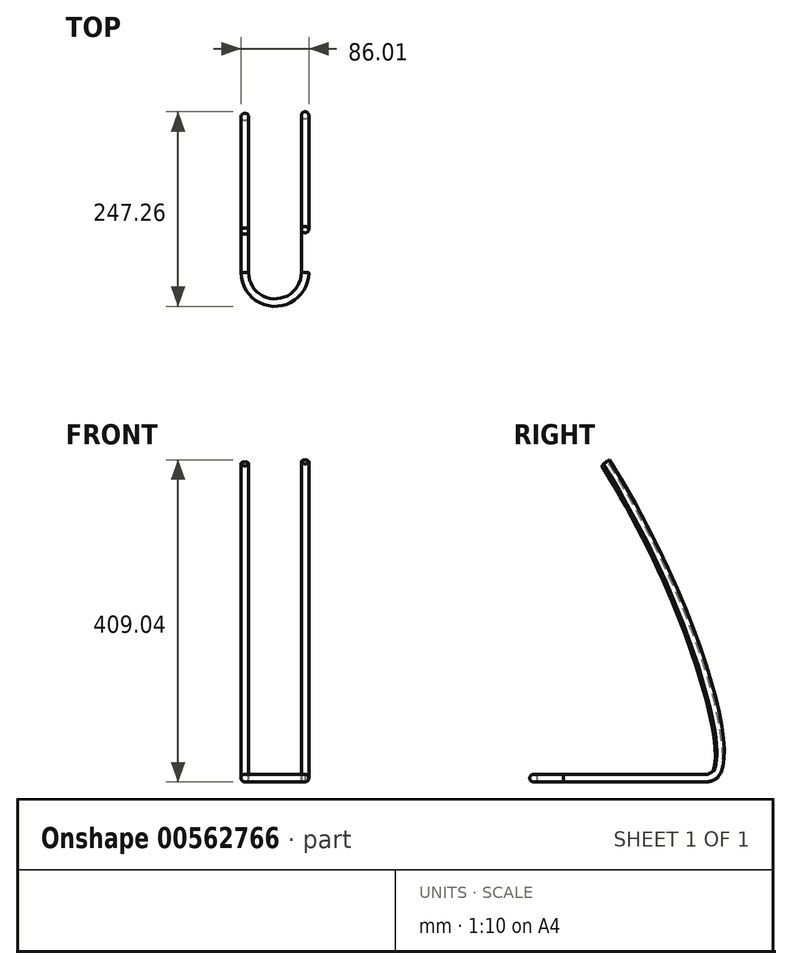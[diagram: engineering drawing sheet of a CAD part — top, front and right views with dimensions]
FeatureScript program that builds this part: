
annotation { "Feature Type Name" : "Feature", "Feature Type Description" : "" }
export const myFeature = defineFeature(function(context is Context, id is Id, definition is map)
    precondition{}
    {
        {
            var Q0;
            Q0=qCreatedBy(makeId("Top.planeOp"),FACE);
            var sketch = newSketch(context, id + "F0", { "sketchPlane" : qUnion([Q0])});
            skArc(sketch, "E0", {"start": v(-46.05, 0) * mm, "mid": v(-7.8, -37.96) * mm, "end": v(30.43, 0) * mm});
            skLineSegment(sketch, "E1", {"start": v(-46.05, 0) * mm, "end": v(-46.05, 180) * mm});
            skLineSegment(sketch, "E2", {"start": v(30.43, 0) * mm, "end": v(30.43, 180) * mm});
            skSolve(sketch);
        }
        {
            var Q0;
            Q0=qCreatedBy(makeId("Front.planeOp"),FACE);
            var sketch = newSketch(context, id + "F1", { "sketchPlane" : qUnion([Q0])});
            skCircle(sketch, "E3", {"center": v(-46.05, 0) * mm, "radius": 4.76 * mm});
            skCircle(sketch, "E4", {"center": v(30.43, 0) * mm, "radius": 4.76 * mm});
            skSolve(sketch);
        }
        {
            var Q0;
            Q0=qCreatedBy(makeId("Right.planeOp"),FACE);
            var Q1;
            Q1=sQuery(id+"F0.wireOp",VERTEX,"E2.end");
            cPlane(context, id + "F2", {"entities" : qUnion([Q0, Q1]), "cplaneType" : CPlaneType.PLANE_POINT, "offset" : 25.4 * mm, "width" : 152.4 * mm, "height" : 152.4 * mm});
        }
        {
            var Q0;
            Q0=qCreatedBy(makeId("Right.planeOp"),FACE);
            var Q1;
            Q1=sQuery(id+"F0.wireOp",VERTEX,"E1.end");
            cPlane(context, id + "F3", {"entities" : qUnion([Q0, Q1]), "cplaneType" : CPlaneType.PLANE_POINT, "offset" : 25.4 * mm, "width" : 152.4 * mm, "height" : 152.4 * mm});
        }
        {
            var Q0;
            Q0=qCreatedBy(id+"F3.planeOp",FACE);
            var sketch = newSketch(context, id + "F4", { "sketchPlane" : qUnion([Q0])});
            skFitSpline(sketch, "E5", {"points": [v(180, 0) * mm, v(193.9, 6.08) * mm, v(52.87, 399.27) * mm], "startDerivative": vector(82.42, 0) * mm, "endDerivative": vector(-398.3, 638.43) * mm});
            skSolve(sketch);
        }
        {
            var Q0;
            Q0=makeQuery(id+"F1.imprint","IMPRINT",FACE,{"disambiguationData":[TD([[makeQuery(id+"F1.imprint","IMPRINT",EDGE,{"derivedFrom":sQuery(id+"F1.wireOp",EDGE,"E3")}),1.0]])]});
            var Q1;
            Q1=sQuery(id+"F4.wireOp",EDGE,"E5");
            var Q2;
            Q2=sQuery(id+"F0.wireOp",EDGE,"E1");
            sweep(context, id + "F5", {"profiles" : qUnion([Q0]), "path" : qUnion([Q1, Q2])});
        }
        {
            var Q0;
            Q0 = qSketchRegion(id + "F1", true);
            var Q1;
            Q1=sQuery(id+"F0.wireOp",EDGE,"E0");
            sweep(context, id + "F6", {"profiles" : qUnion([Q0]), "path" : qUnion([Q1])});
        }
        {
            var Q0;
            Q0=makeQuery(id+"F6.opSweep","SWEPT_BODY",BODY,{"disambiguationData":[OSD([sQuery(id+"F0.wireOp",EDGE,"E0"),sQuery(id+"F1.wireOp",EDGE,"E4")])]});
            deleteBodies(context, id + "F7", {"entities" : qUnion([Q0])});
        }
        {
            var Q0;
            Q0=makeQuery(id+"F1.imprint","IMPRINT",FACE,{"disambiguationData":[TD([[makeQuery(id+"F1.imprint","IMPRINT",EDGE,{"derivedFrom":sQuery(id+"F1.wireOp",EDGE,"E4")}),1.0]])]});
            var Q1;
            Q1=sQuery(id+"F0.wireOp",EDGE,"E2");
            sweep(context, id + "F8", {"operationType" : NewBodyOperationType.ADD, "profiles" : qUnion([Q0]), "path" : qUnion([Q1])});
        }
        {
            var Q0;
            Q0=qCreatedBy(id+"F2.planeOp",FACE);
            var sketch = newSketch(context, id + "F9", { "sketchPlane" : qUnion([Q0])});
            skFitSpline(sketch, "E6", {"points": [v(180, 0) * mm, v(195.72, 8.57) * mm, v(54.7, 401.76) * mm], "startDerivative": vector(82.42, 0) * mm, "endDerivative": vector(-398.3, 638.43) * mm});
            skSolve(sketch);
        }
        {
            var Q0;
            Q0=makeQuery(id+"F8.opSweep","CAP_FACE",FACE,{"disambiguationData":[OSD([sQuery(id+"F0.wireOp",VERTEX,"E2.end"),sQuery(id+"F1.wireOp",EDGE,"E4")])],"isStart":false});
            var Q1;
            Q1=sQuery(id+"F9.wireOp",EDGE,"E6");
            sweep(context, id + "F10", {"operationType" : NewBodyOperationType.ADD, "profiles" : qUnion([Q0]), "path" : qUnion([Q1])});
        }
    });
